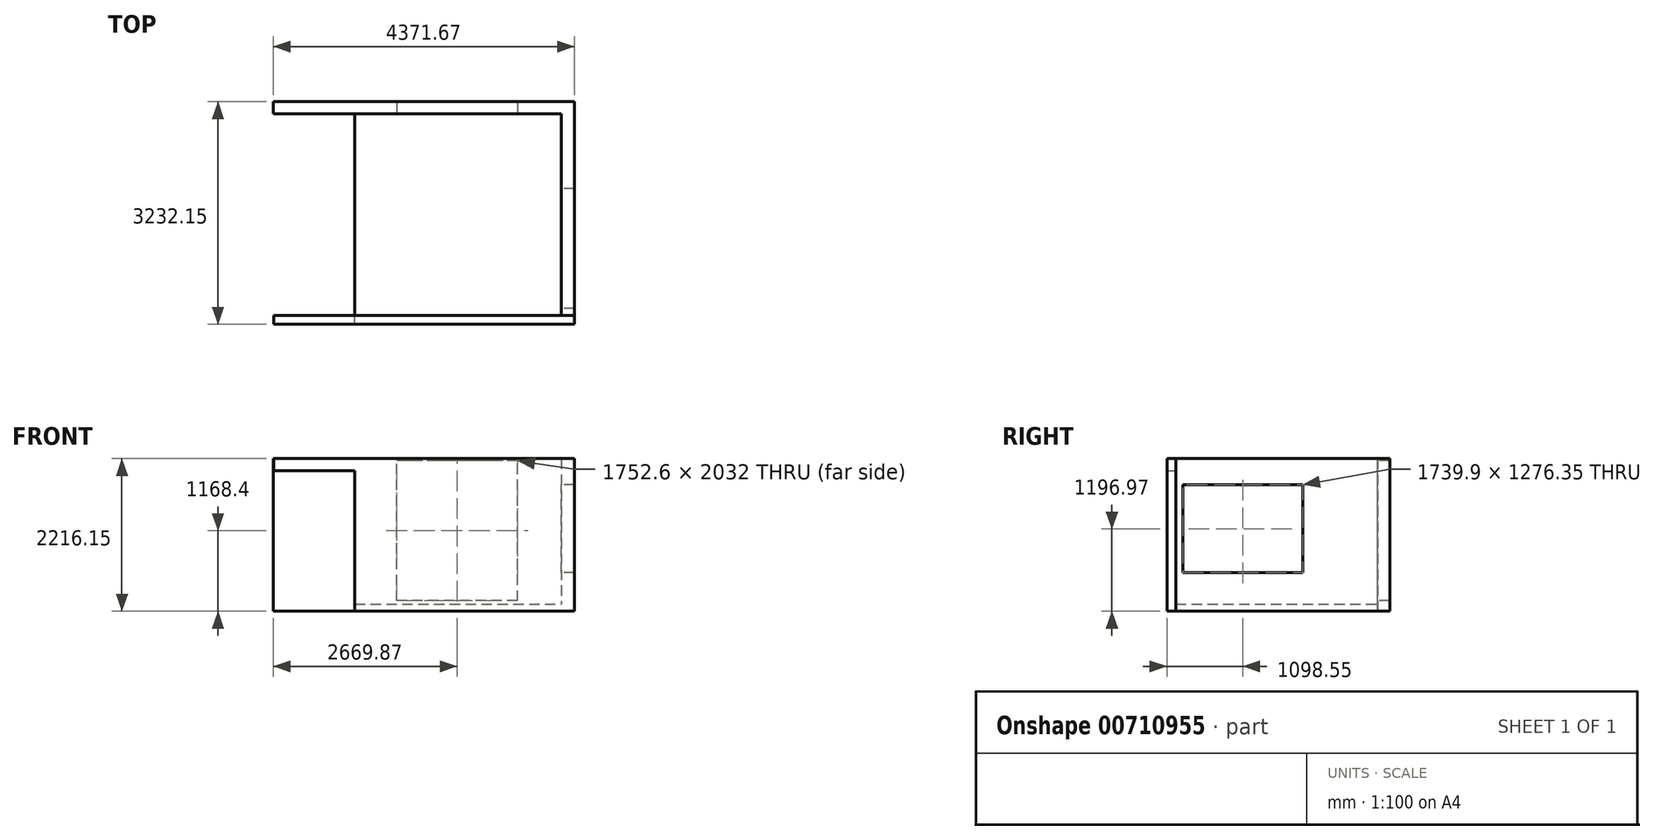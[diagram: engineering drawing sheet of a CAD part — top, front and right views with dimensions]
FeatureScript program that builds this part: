
annotation { "Feature Type Name" : "Feature", "Feature Type Description" : "" }
export const myFeature = defineFeature(function(context is Context, id is Id, definition is map)
    precondition{}
    {
        {
            var Q0;
            Q0=qCreatedBy(makeId("Top.planeOp"),FACE);
            var sketch = newSketch(context, id + "F0", { "sketchPlane" : qUnion([Q0])});
            skLineSegment(sketch, "E0.bottom", {"start": v(-1215.97, -1457.09) * mm, "end": v(1781.23, -1457.09) * mm});
            skLineSegment(sketch, "E0.top", {"start": v(-1215.97, 1470.26) * mm, "end": v(1781.23, 1470.26) * mm});
            skLineSegment(sketch, "E0.left", {"start": v(-1215.97, -1457.09) * mm, "end": v(-1215.97, 1470.26) * mm});
            skLineSegment(sketch, "E0.right", {"start": v(1781.23, -1457.09) * mm, "end": v(1781.23, 1470.26) * mm});
            skSolve(sketch);
        }
        {
            var Q0;
            Q0 = qSketchRegion(id + "F0", true);
            extrude(context, id + "F1", {"entities" : qUnion([Q0]), "depth" : 101.6 * mm, "offsetDistance" : 25.4 * mm});
        }
        {
            var Q0;
            Q0=makeQuery(id+"F1.opExtrude","SWEPT_FACE",FACE,{"disambiguationData":[OSD([sQuery(id+"F0.wireOp",EDGE,"E0.right")])]});
            var sketch = newSketch(context, id + "F2", { "sketchPlane" : qUnion([Q0])});
            skLineSegment(sketch, "E1.bottom", {"start": v(-1457.09, 0) * mm, "end": v(1470.26, 0) * mm});
            skLineSegment(sketch, "E1.top", {"start": v(-1457.09, 2216.15) * mm, "end": v(1470.26, 2216.15) * mm});
            skLineSegment(sketch, "E1.left", {"start": v(-1457.09, 0) * mm, "end": v(-1457.09, 2216.15) * mm});
            skLineSegment(sketch, "E1.right", {"start": v(1470.26, 0) * mm, "end": v(1470.26, 2216.15) * mm});
            skSolve(sketch);
        }
        {
            var Q0;
            Q0 = qSketchRegion(id + "F2", true);
            extrude(context, id + "F3", {"entities" : qUnion([Q0]), "operationType" : NewBodyOperationType.ADD, "depth" : 190.5 * mm, "offsetDistance" : 25.4 * mm});
        }
        {
            var Q0;
            Q0=makeQuery(id+"F3.opExtrude","CAP_FACE",FACE,{"disambiguationData":[OSD([sQuery(id+"F2.wireOp",EDGE,"E1.bottom"),sQuery(id+"F2.wireOp",EDGE,"E1.top"),sQuery(id+"F2.wireOp",EDGE,"E1.left"),sQuery(id+"F2.wireOp",EDGE,"E1.right")])],"isStart":true});
            var sketch = newSketch(context, id + "F4", { "sketchPlane" : qUnion([Q0])});
            skLineSegment(sketch, "E2.bottom", {"start": v(1355.49, 558.8) * mm, "end": v(-384.41, 558.8) * mm});
            skLineSegment(sketch, "E2.top", {"start": v(1355.49, 1835.15) * mm, "end": v(-384.41, 1835.15) * mm});
            skLineSegment(sketch, "E2.left", {"start": v(1355.49, 558.8) * mm, "end": v(1355.49, 1835.15) * mm});
            skLineSegment(sketch, "E2.right", {"start": v(-384.41, 558.8) * mm, "end": v(-384.41, 1835.15) * mm});
            skSolve(sketch);
        }
        {
            var Q0;
            Q0=makeQuery(id+"F4.imprint","IMPRINT",FACE,{"disambiguationData":[TD([[makeQuery(id+"F4.imprint","IMPRINT",EDGE,{"derivedFrom":sQuery(id+"F4.wireOp",EDGE,"E2.bottom")}),-1.0]])]});
            extrude(context, id + "F5", {"entities" : qUnion([Q0]), "operationType" : NewBodyOperationType.REMOVE, "endBound" : BoundingType.UP_TO_NEXT, "oppositeDirection" : true, "depth" : 25.4 * mm, "offsetDistance" : 25.4 * mm});
        }
        {
            var Q0;
            Q0=makeQuery(id+"F3.boolean.opBoolean","MERGE",FACE,{"derivedFrom":[makeQuery(id+"F1.opExtrude","SWEPT_FACE",FACE,{"disambiguationData":[OSD([sQuery(id+"F0.wireOp",EDGE,"E0.bottom")])]}),makeQuery(id+"F3.opExtrude","SWEPT_FACE",FACE,{"disambiguationData":[OSD([sQuery(id+"F2.wireOp",EDGE,"E1.left")])]})]});
            var sketch = newSketch(context, id + "F6", { "sketchPlane" : qUnion([Q0])});
            skLineSegment(sketch, "E3.bottom", {"start": v(1971.73, 0) * mm, "end": v(-2391.23, 0) * mm});
            skLineSegment(sketch, "E3.top", {"start": v(1971.73, 2216.15) * mm, "end": v(-2391.23, 2216.15) * mm});
            skLineSegment(sketch, "E3.left", {"start": v(1971.73, 0) * mm, "end": v(1971.73, 2216.15) * mm});
            skLineSegment(sketch, "E3.right", {"start": v(-2391.23, 0) * mm, "end": v(-2391.23, 2216.15) * mm});
            skSolve(sketch);
        }
        {
            var Q0;
            {var subQ2=sQuery(id+"F6.wireOp",EDGE,"E3.left");Q0=makeQuery(id+"F6.imprint","IMPRINT",FACE,{"disambiguationData":[TD([[makeQuery(id+"F6.imprint","IMPRINT",EDGE,{"derivedFrom":subQ2}),-1.0]])]});}
            var Q1;
            {var subQ0=sQuery(id+"F6.wireOp",EDGE,"E3.right");Q1=makeQuery(id+"F6.imprint","IMPRINT",FACE,{"disambiguationData":[TD([[makeQuery(id+"F6.imprint","IMPRINT",EDGE,{"derivedFrom":subQ0}),-1.0]])]});}
            extrude(context, id + "F7", {"entities" : qUnion([Q0, Q1]), "depth" : 127 * mm, "offsetDistance" : 25.4 * mm});
        }
        {
            var Q0;
            Q0=makeQuery(id+"F7.opExtrude","CAP_FACE",FACE,{"disambiguationData":[OSD([sQuery(id+"F6.wireOp",EDGE,"E3.bottom"),sQuery(id+"F6.wireOp",EDGE,"E3.top"),sQuery(id+"F6.wireOp",EDGE,"E3.left"),sQuery(id+"F6.wireOp",EDGE,"E3.right")])],"isStart":true});
            var sketch = newSketch(context, id + "F8", { "sketchPlane" : qUnion([Q0])});
            skLineSegment(sketch, "E4", {"start": v(1215.98, 0) * mm, "end": v(1215.98, 2041.53) * mm});
            skLineSegment(sketch, "E5", {"start": v(1215.98, 2041.53) * mm, "end": v(2391.23, 2041.53) * mm});
            skSolve(sketch);
        }
        {
            var Q0;
            {var subQ0=sQuery(id+"F8.wireOp",EDGE,"E4");Q0=makeQuery(id+"F8.imprint","IMPRINT",FACE,{"disambiguationData":[TD([[makeQuery(id+"F8.imprint","IMPRINT",EDGE,{"derivedFrom":subQ0}),-1.0]])]});}
            extrude(context, id + "F9", {"entities" : qUnion([Q0]), "operationType" : NewBodyOperationType.REMOVE, "endBound" : BoundingType.UP_TO_NEXT, "oppositeDirection" : true, "depth" : 25.4 * mm, "offsetDistance" : 25.4 * mm});
        }
        {
            var Q0;
            Q0=makeQuery(id+"F3.boolean.opBoolean","MERGE",FACE,{"derivedFrom":[makeQuery(id+"F1.opExtrude","SWEPT_FACE",FACE,{"disambiguationData":[OSD([sQuery(id+"F0.wireOp",EDGE,"E0.top")])]}),makeQuery(id+"F3.opExtrude","SWEPT_FACE",FACE,{"disambiguationData":[OSD([sQuery(id+"F2.wireOp",EDGE,"E1.right")])]})]});
            var sketch = newSketch(context, id + "F10", { "sketchPlane" : qUnion([Q0])});
            skLineSegment(sketch, "E6.bottom", {"start": v(-1971.73, 0) * mm, "end": v(2399.94, 0) * mm});
            skLineSegment(sketch, "E6.top", {"start": v(-1971.73, 2216.15) * mm, "end": v(2399.94, 2216.15) * mm});
            skLineSegment(sketch, "E6.left", {"start": v(-1971.73, 0) * mm, "end": v(-1971.73, 2216.15) * mm});
            skLineSegment(sketch, "E6.right", {"start": v(2399.94, 0) * mm, "end": v(2399.94, 2216.15) * mm});
            skSolve(sketch);
        }
        {
            var Q0;
            {var subQ0=sQuery(id+"F10.wireOp",EDGE,"E6.right");Q0=makeQuery(id+"F10.imprint","IMPRINT",FACE,{"disambiguationData":[TD([[makeQuery(id+"F10.imprint","IMPRINT",EDGE,{"derivedFrom":subQ0}),1.0]])]});}
            var Q1;
            {var subQ2=sQuery(id+"F10.wireOp",EDGE,"E6.left");Q1=makeQuery(id+"F10.imprint","IMPRINT",FACE,{"disambiguationData":[TD([[makeQuery(id+"F10.imprint","IMPRINT",EDGE,{"derivedFrom":subQ2}),1.0]])]});}
            extrude(context, id + "F11", {"entities" : qUnion([Q0, Q1]), "operationType" : NewBodyOperationType.ADD, "depth" : 177.8 * mm, "offsetDistance" : 25.4 * mm});
        }
        {
            var Q0;
            Q0=makeQuery(id+"F11.opExtrude","CAP_FACE",FACE,{"disambiguationData":[OSD([sQuery(id+"F10.wireOp",EDGE,"E6.bottom"),sQuery(id+"F10.wireOp",EDGE,"E6.top"),sQuery(id+"F10.wireOp",EDGE,"E6.left"),sQuery(id+"F10.wireOp",EDGE,"E6.right")])],"isStart":true});
            var sketch = newSketch(context, id + "F12", { "sketchPlane" : qUnion([Q0])});
            skLineSegment(sketch, "E7.bottom", {"start": v(1146.23, 152.4) * mm, "end": v(-606.37, 152.4) * mm});
            skLineSegment(sketch, "E7.top", {"start": v(1146.23, 2184.4) * mm, "end": v(-606.37, 2184.4) * mm});
            skLineSegment(sketch, "E7.left", {"start": v(1146.23, 152.4) * mm, "end": v(1146.23, 2184.4) * mm});
            skLineSegment(sketch, "E7.right", {"start": v(-606.37, 152.4) * mm, "end": v(-606.37, 2184.4) * mm});
            skSolve(sketch);
        }
        {
            var Q0;
            Q0=makeQuery(id+"F12.imprint","IMPRINT",FACE,{"disambiguationData":[TD([[makeQuery(id+"F12.imprint","IMPRINT",EDGE,{"derivedFrom":sQuery(id+"F12.wireOp",EDGE,"E7.bottom")}),-1.0]])]});
            extrude(context, id + "F13", {"entities" : qUnion([Q0]), "operationType" : NewBodyOperationType.REMOVE, "endBound" : BoundingType.UP_TO_NEXT, "oppositeDirection" : true, "depth" : 25.4 * mm, "offsetDistance" : 25.4 * mm});
        }
    });
